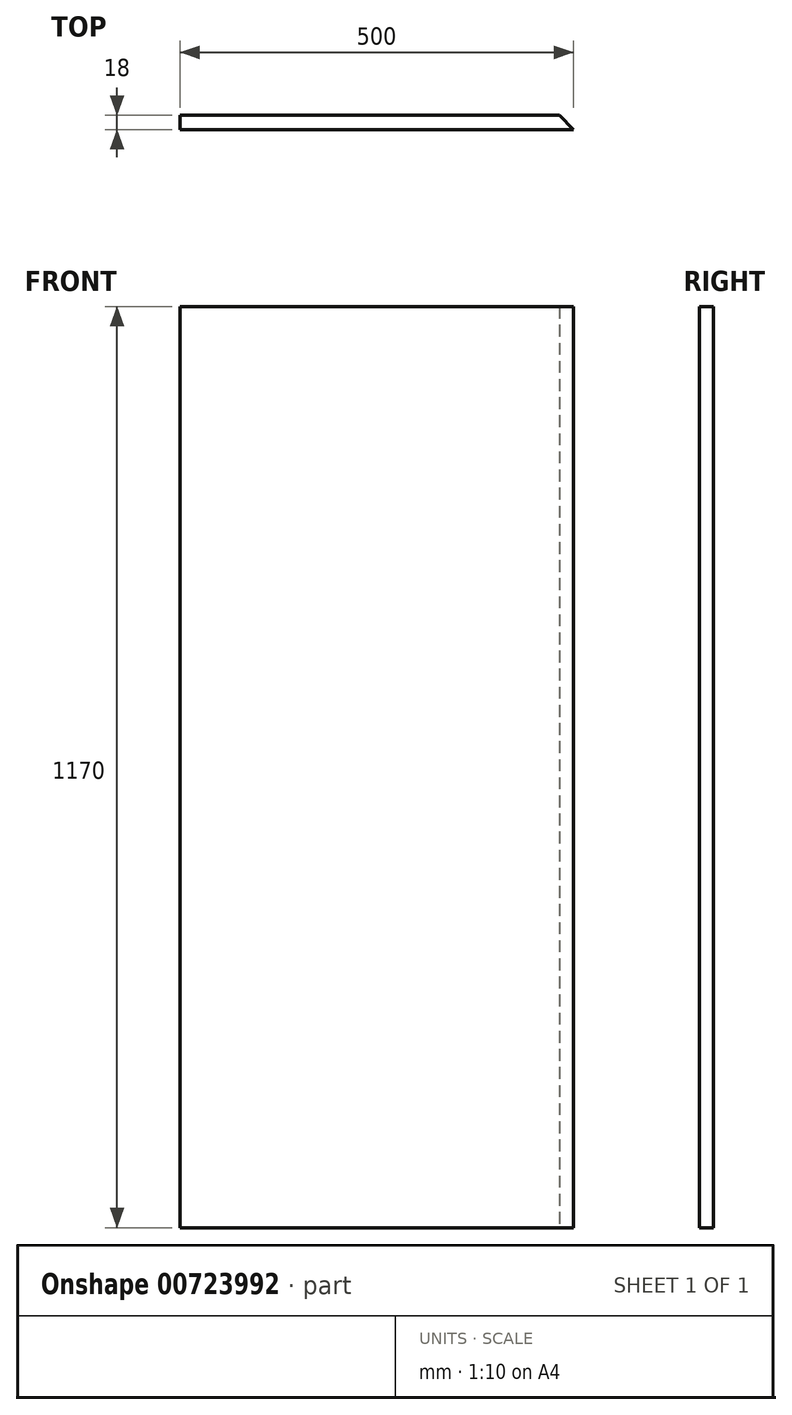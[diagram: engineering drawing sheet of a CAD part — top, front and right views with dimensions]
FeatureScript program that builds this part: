
annotation { "Feature Type Name" : "Feature", "Feature Type Description" : "" }
export const myFeature = defineFeature(function(context is Context, id is Id, definition is map)
    precondition{}
    {
        {
            var Q0;
            Q0=qCreatedBy(makeId("Front.planeOp"),FACE);
            var sketch = newSketch(context, id + "F0", { "sketchPlane" : qUnion([Q0])});
            skLineSegment(sketch, "E0.bottom", {"start": v(-250, 585) * mm, "end": v(250, 585) * mm});
            skLineSegment(sketch, "E0.top", {"start": v(-250, -585) * mm, "end": v(250, -585) * mm});
            skLineSegment(sketch, "E0.left", {"start": v(-250, 585) * mm, "end": v(-250, -585) * mm});
            skLineSegment(sketch, "E0.right", {"start": v(250, 585) * mm, "end": v(250, -585) * mm});
            skLineSegment(sketch, "E1", {"start": v(-250, 585) * mm, "end": v(250, -585) * mm});
            skLineSegment(sketch, "E2", {"start": v(250, 585) * mm, "end": v(-250, -585) * mm});
            skSolve(sketch);
        }
        {
            var Q0;
            Q0=qSketchRegion(id+"F0",true);
            extrude(context, id + "F1", {"entities" : qUnion([Q0]), "depth" : 18 * mm, "offsetDistance" : 25 * mm});
        }
        {
            var Q0;
            Q0=makeQuery(id+"F1.opExtrude","CAP_EDGE",EDGE,{"disambiguationData":[OSD([sQuery(id+"F0.wireOp",EDGE,"E0.right")])],"isStart":true});
            chamfer(context, id + "F2", {"entities" : qUnion([Q0]), "width" : 18 * mm, "tangentPropagation" : true});
        }
    });
